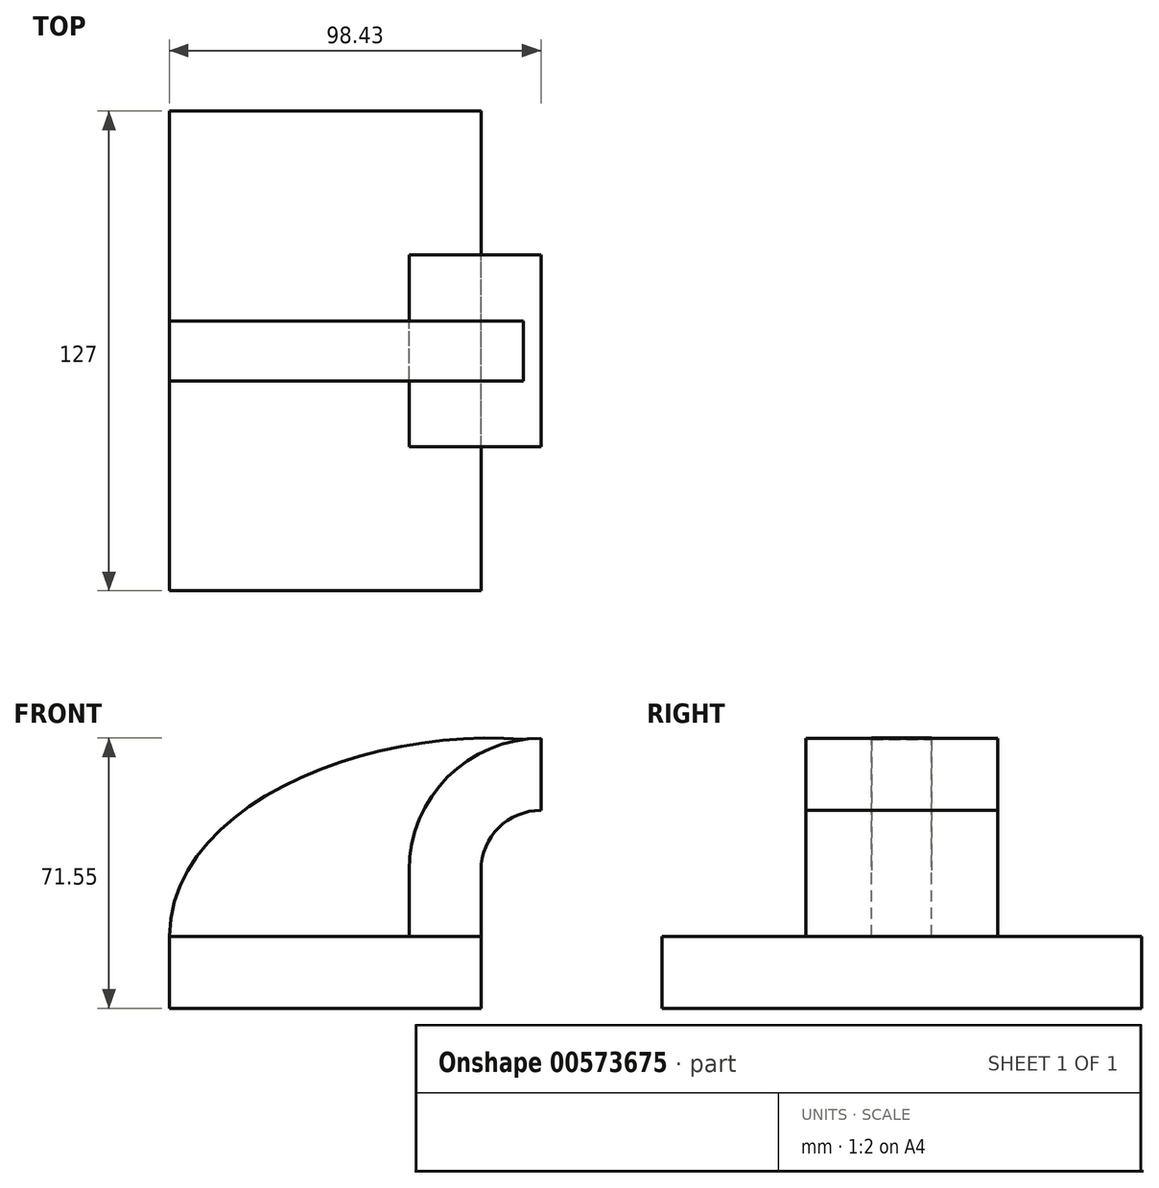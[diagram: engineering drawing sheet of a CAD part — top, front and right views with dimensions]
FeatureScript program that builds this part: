
annotation { "Feature Type Name" : "Feature", "Feature Type Description" : "" }
export const myFeature = defineFeature(function(context is Context, id is Id, definition is map)
    precondition{}
    {
        {
            var Q0;
            Q0=qCreatedBy(makeId("Front.planeOp"),FACE);
            var sketch = newSketch(context, id + "F0", { "sketchPlane" : qUnion([Q0])});
            skLineSegment(sketch, "E0.bottom", {"start": v(-41.28, 9.52) * mm, "end": v(41.27, 9.53) * mm});
            skLineSegment(sketch, "E0.top", {"start": v(-41.28, -9.53) * mm, "end": v(41.28, -9.53) * mm});
            skLineSegment(sketch, "E0.left", {"start": v(-41.28, 9.52) * mm, "end": v(-41.27, -9.53) * mm});
            skLineSegment(sketch, "E0.right", {"start": v(41.28, 9.53) * mm, "end": v(41.28, -9.52) * mm});
            skPoint(sketch, "E0.middle", {"position": v(0, 0) * mm});
            skLineSegment(sketch, "E1.bottom", {"start": v(57.15, 66.67) * mm, "end": v(107.95, 66.67) * mm});
            skLineSegment(sketch, "E1.top", {"start": v(57.15, 38.1) * mm, "end": v(107.95, 38.1) * mm});
            skLineSegment(sketch, "E1.left", {"start": v(57.15, 66.67) * mm, "end": v(57.15, 38.1) * mm});
            skLineSegment(sketch, "E1.right", {"start": v(107.95, 66.67) * mm, "end": v(107.95, 38.1) * mm});
            skPoint(sketch, "E1.middle", {"position": v(82.55, 52.39) * mm});
            skLineSegment(sketch, "E2", {"start": v(41.27, 9.53) * mm, "end": v(41.27, 27) * mm});
            skArc(sketch, "E3", {"start": v(41.27, 27) * mm, "mid": v(45.92, 38.23) * mm, "end": v(57.15, 42.88) * mm});
            skLineSegment(sketch, "E4", {"start": v(57.15, 42.88) * mm, "end": v(107.95, 42.88) * mm});
            skLineSegment(sketch, "E5", {"start": v(107.95, 42.88) * mm, "end": v(87.66, 42.88) * mm});
            skArc(sketch, "E6.0", {"start": v(22.22, 27) * mm, "mid": v(32.45, 51.7) * mm, "end": v(57.15, 61.93) * mm});
            skLineSegment(sketch, "E6.1", {"start": v(22.22, 9.53) * mm, "end": v(22.22, 27) * mm});
            skFitSpline(sketch, "E7", {"points": [v(-41.28, 9.52) * mm, v(52.51, 61.62) * mm], "startDerivative": vector(2, 108.24) * mm, "endDerivative": vector(117.54, -10.45) * mm});
            skLineSegment(sketch, "E8", {"start": v(82.55, 38.1) * mm, "end": v(82.55, 66.67) * mm});
            skSolve(sketch);
        }
        {
            var Q0;
            Q0=makeQuery(id+"F0.imprint","IMPRINT",FACE,{"disambiguationData":[TD([[makeQuery(id+"F0.imprint","IMPRINT",EDGE,{"derivedFrom":sQuery(id+"F0.wireOp",EDGE,"E0.top")}),1.0]])]});
            extrude(context, id + "F1", {"entities" : qUnion([Q0]), "endBound" : BoundingType.SYMMETRIC, "depth" : 127 * mm, "offsetDistance" : 25.4 * mm});
        }
        {
            var Q0;
            {var subQ0=sQuery(id+"F0.wireOp",EDGE,"E2");Q0=makeQuery(id+"F0.imprint","IMPRINT",FACE,{"disambiguationData":[TD([[makeQuery(id+"F0.imprint","IMPRINT",EDGE,{"derivedFrom":subQ0}),1.0]])]});}
            extrude(context, id + "F2", {"entities" : qUnion([Q0]), "endBound" : BoundingType.SYMMETRIC, "depth" : 50.8 * mm, "offsetDistance" : 25.4 * mm});
        }
        {
            var Q0;
            {var subQ2=sQuery(id+"F0.wireOp",EDGE,"E6.1");Q0=makeQuery(id+"F0.imprint","IMPRINT",FACE,{"disambiguationData":[TD([[makeQuery(id+"F0.imprint","IMPRINT",EDGE,{"derivedFrom":subQ2}),1.0]])]});}
            extrude(context, id + "F3", {"entities" : qUnion([Q0]), "endBound" : BoundingType.SYMMETRIC, "depth" : 15.88 * mm, "offsetDistance" : 25.4 * mm});
        }
    });
